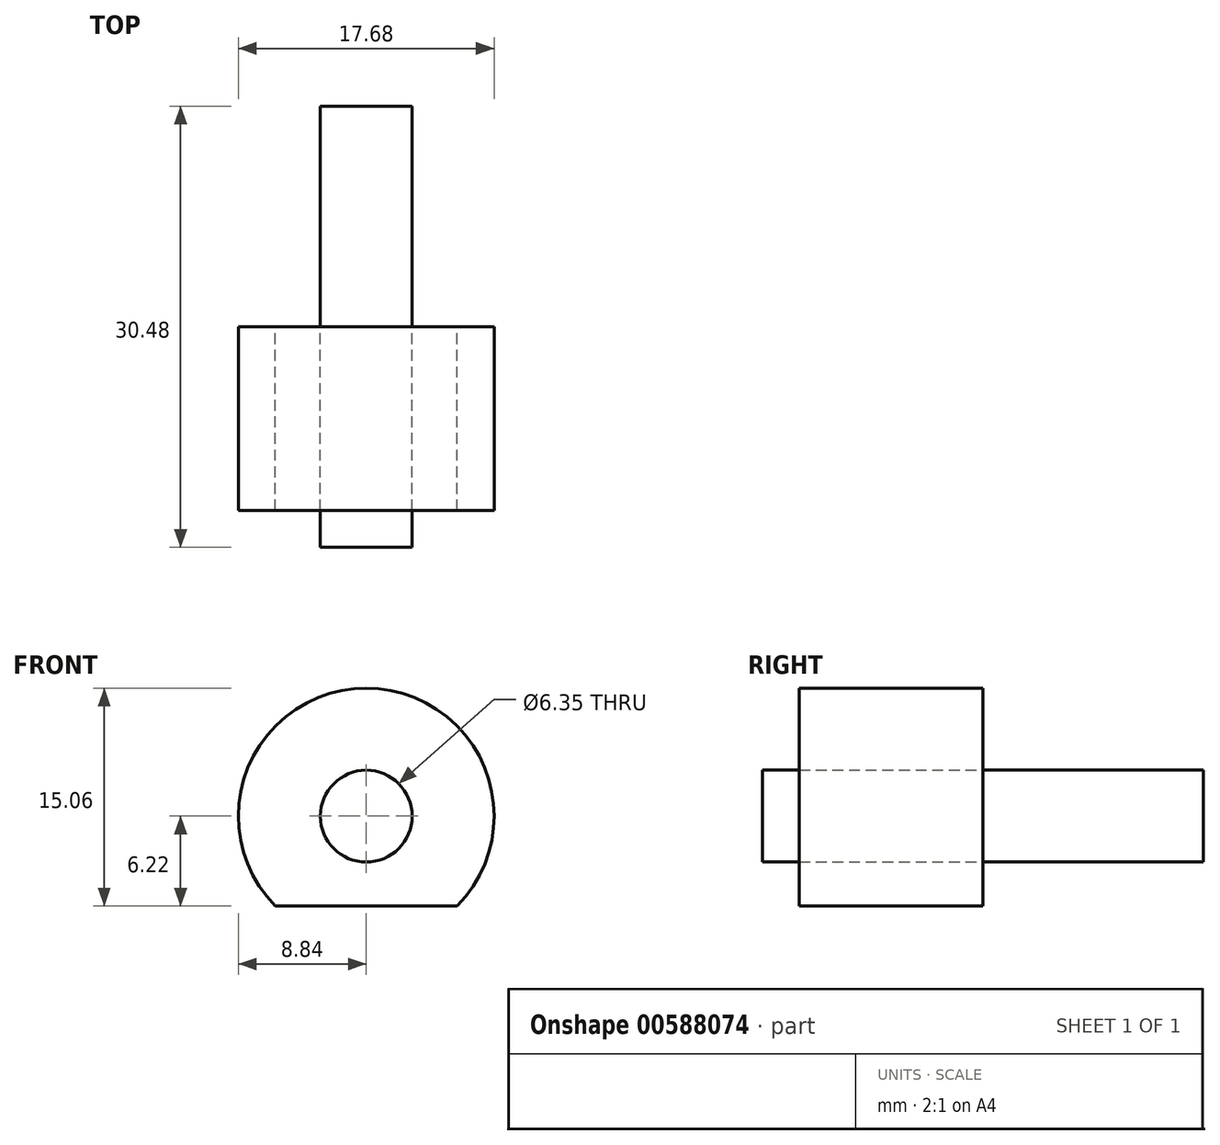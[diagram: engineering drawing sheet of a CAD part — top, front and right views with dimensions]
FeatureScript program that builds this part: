
annotation { "Feature Type Name" : "Feature", "Feature Type Description" : "" }
export const myFeature = defineFeature(function(context is Context, id is Id, definition is map)
    precondition{}
    {
        {
            var Q0;
            Q0=qCreatedBy(makeId("Front.planeOp"),FACE);
            var sketch = newSketch(context, id + "F0", { "sketchPlane" : qUnion([Q0])});
            skCircle(sketch, "E0", {"center": v(0, 0) * mm, "radius": 3.18 * mm});
            skArc(sketch, "E1", {"start": v(-6.28, -6.22) * mm, "mid": v(0, 8.84) * mm, "end": v(6.28, -6.22) * mm});
            skLineSegment(sketch, "E2", {"start": v(-6.28, -6.22) * mm, "end": v(6.28, -6.22) * mm});
            skSolve(sketch);
        }
        {
            var Q0;
            Q0=makeQuery(id+"F0.imprint","IMPRINT",FACE,{"disambiguationData":[TD([[makeQuery(id+"F0.imprint","IMPRINT",EDGE,{"derivedFrom":sQuery(id+"F0.wireOp",EDGE,"E0")}),1.0]])]});
            var sketch = newSketch(context, id + "F1", { "sketchPlane" : qUnion([Q0])});
            skSolve(sketch);
        }
        {
            var Q0;
            Q0=makeQuery(id+"F0.imprint","IMPRINT",FACE,{"disambiguationData":[TD([[makeQuery(id+"F0.imprint","IMPRINT",EDGE,{"derivedFrom":sQuery(id+"F0.wireOp",EDGE,"E0")}),-1.0]])]});
            extrude(context, id + "F2", {"entities" : qUnion([Q0]), "depth" : 12.7 * mm, "offsetDistance" : 25.4 * mm});
        }
        {
            var Q0;
            Q0 = qSketchRegion(id + "F1", true);
            var Q1;
            Q1=makeQuery(id+"F1.imprint","IMPRINT",FACE,{"disambiguationData":[TD([[makeQuery(id+"F1.imprint","IMPRINT",EDGE,{"derivedFrom":makeQuery(id+"F0.imprint","IMPRINT",EDGE,{"derivedFrom":sQuery(id+"F0.wireOp",EDGE,"E0")})}),1.0]])]});
            extrude(context, id + "F3", {"entities" : qUnion([Q0, Q1]), "endBound" : BoundingType.SYMMETRIC, "oppositeDirection" : true, "depth" : 30.48 * mm, "offsetDistance" : 25.4 * mm});
        }
    });
